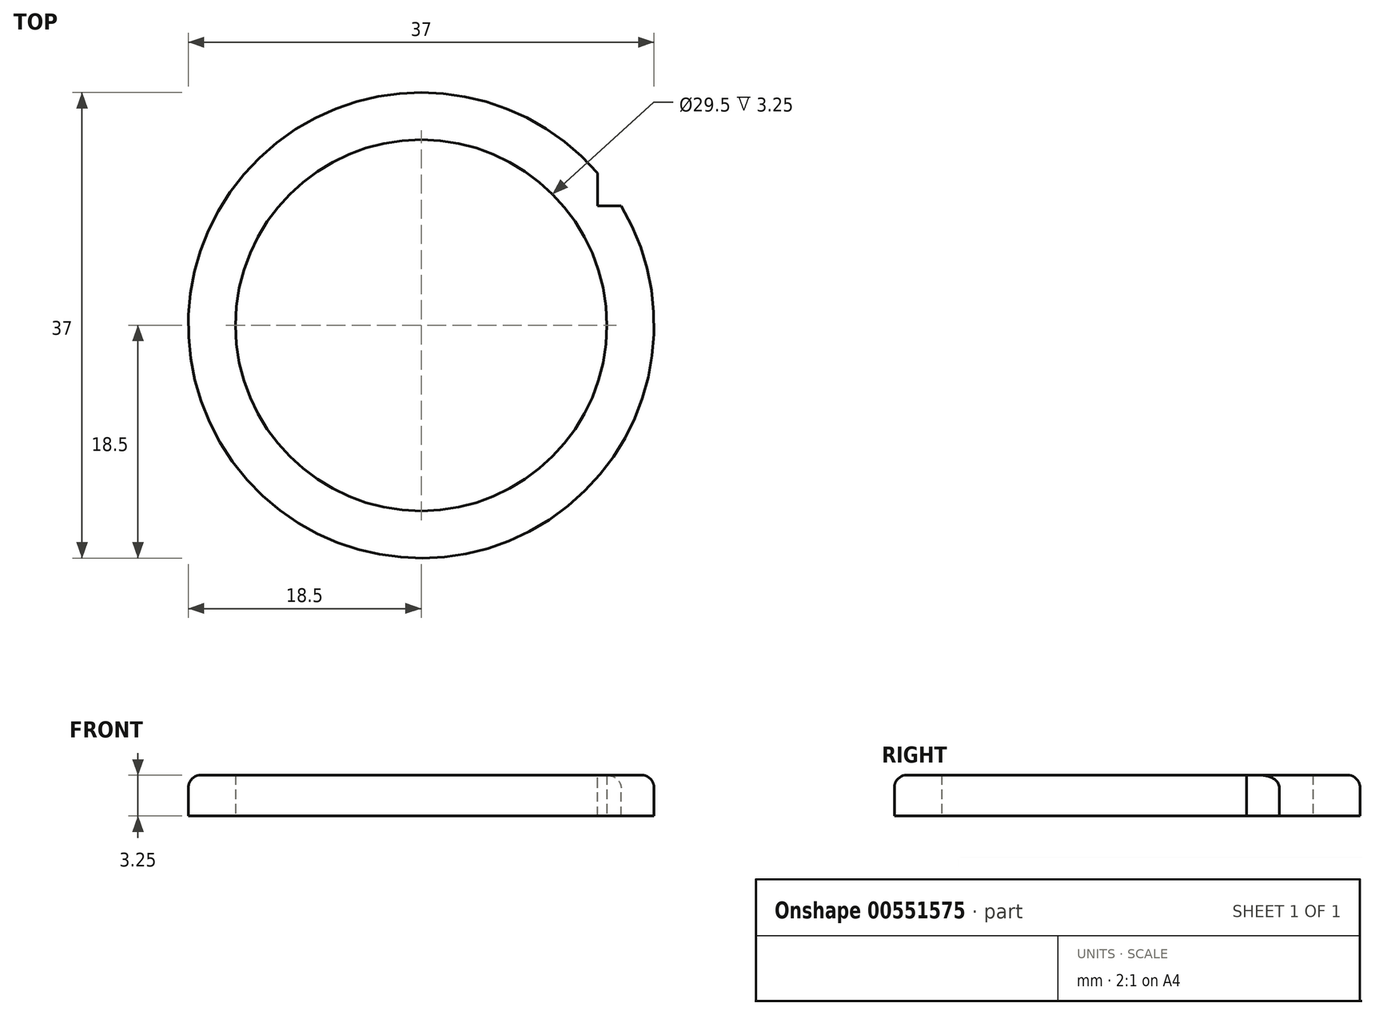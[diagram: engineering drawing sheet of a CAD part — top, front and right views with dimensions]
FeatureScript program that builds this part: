
annotation { "Feature Type Name" : "Feature", "Feature Type Description" : "" }
export const myFeature = defineFeature(function(context is Context, id is Id, definition is map)
    precondition{}
    {
        {
            var Q0;
            Q0=qCreatedBy(makeId("Top.planeOp"),FACE);
            var sketch = newSketch(context, id + "F0", { "sketchPlane" : qUnion([Q0])});
            skCircle(sketch, "E0", {"center": v(0, 0) * mm, "radius": 14.75 * mm});
            skCircle(sketch, "E1", {"center": v(0, 0) * mm, "radius": 18.5 * mm});
            skSolve(sketch);
        }
        {
            var Q0;
            Q0 = qSketchRegion(id + "F0", true);
            extrude(context, id + "F1", {"entities" : qUnion([Q0]), "depth" : 3.25 * mm, "offsetDistance" : 25 * mm});
        }
        {
            var Q0;
            Q0=makeQuery(id+"F1.opExtrude","CAP_FACE",FACE,{"disambiguationData":[OSD([sQuery(id+"F0.wireOp",EDGE,"E0"),sQuery(id+"F0.wireOp",EDGE,"E1")])],"isStart":false});
            var sketch = newSketch(context, id + "F2", { "sketchPlane" : qUnion([Q0])});
            skLineSegment(sketch, "E2.bottom", {"start": v(20.38, 9.5) * mm, "end": v(14, 9.5) * mm});
            skLineSegment(sketch, "E2.top", {"start": v(20.38, 15.88) * mm, "end": v(14, 15.88) * mm});
            skLineSegment(sketch, "E2.left", {"start": v(20.38, 9.5) * mm, "end": v(20.38, 15.88) * mm});
            skLineSegment(sketch, "E2.right", {"start": v(14, 9.5) * mm, "end": v(14, 15.88) * mm});
            skSolve(sketch);
        }
        {
            var Q0;
            {var subQ0=sQuery(id+"F2.wireOp",EDGE,"E2.right");var subQ1=sQuery(id+"F2.wireOp",EDGE,"E2.bottom");var subQ2=makeQuery(id+"F2.imprint","INTERSECT",VERTEX,{"derivedFrom":[subQ1,subQ0]});Q0=makeQuery(id+"F2.imprint","IMPRINT",FACE,{"disambiguationData":[TD([[makeQuery(id+"F2.imprint","IMPRINT",EDGE,{"disambiguationData":[TD([[subQ2,1.0]])],"derivedFrom":subQ1}),-1.0]])]});}
            extrude(context, id + "F3", {"entities" : qUnion([Q0]), "operationType" : NewBodyOperationType.REMOVE, "oppositeDirection" : true, "depth" : 25 * mm, "offsetDistance" : 25 * mm});
        }
        {
            var Q0;
            Q0=makeQuery(id+"F1.opExtrude","CAP_EDGE",EDGE,{"disambiguationData":[OSD([sQuery(id+"F0.wireOp",EDGE,"E1")])],"isStart":false});
            fillet(context, id + "F4", {"entities" : qUnion([Q0]), "radius" : 1 * mm, "tangentPropagation" : true, "allowEdgeOverflow" : false});
        }
    });
